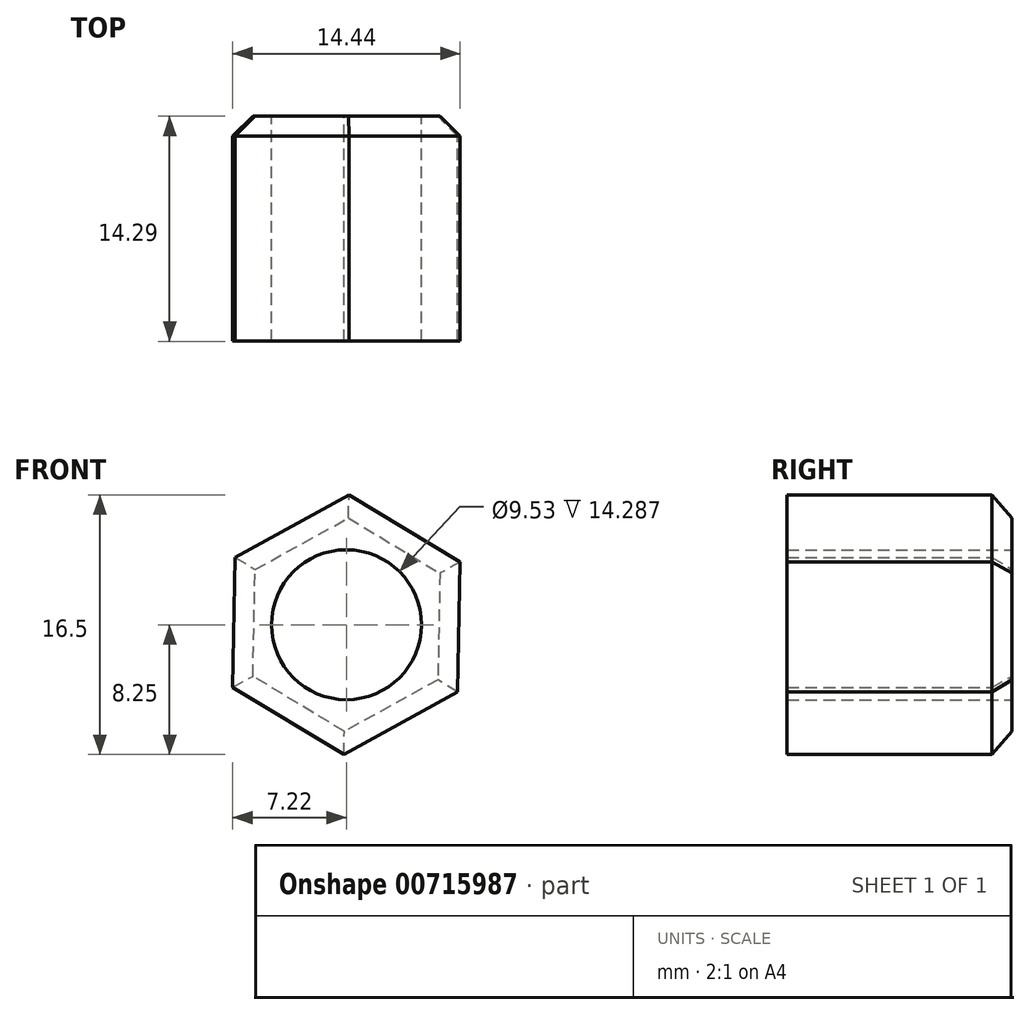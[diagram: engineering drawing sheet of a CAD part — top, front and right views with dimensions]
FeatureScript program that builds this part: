
annotation { "Feature Type Name" : "Feature", "Feature Type Description" : "" }
export const myFeature = defineFeature(function(context is Context, id is Id, definition is map)
    precondition{}
    {
        {
            var Q0;
            Q0=qCreatedBy(makeId("Front.planeOp"),FACE);
            var sketch = newSketch(context, id + "F0", { "sketchPlane" : qUnion([Q0])});
            skCircle(sketch, "E0.cCircle", {"center": v(0, 0) * mm, "radius": 7.14 * mm, "construction": true});
            skLineSegment(sketch, "E0.0", {"start": v(0.16, 8.25) * mm, "end": v(7.22, 3.98) * mm});
            skLineSegment(sketch, "E0.1", {"start": v(7.22, 3.98) * mm, "end": v(7.06, -4.26) * mm});
            skLineSegment(sketch, "E0.2", {"start": v(7.06, -4.26) * mm, "end": v(-0.16, -8.25) * mm});
            skLineSegment(sketch, "E0.3", {"start": v(-0.16, -8.25) * mm, "end": v(-7.22, -3.98) * mm});
            skLineSegment(sketch, "E0.4", {"start": v(-7.22, -3.98) * mm, "end": v(-7.06, 4.26) * mm});
            skLineSegment(sketch, "E0.5", {"start": v(-7.06, 4.26) * mm, "end": v(0.16, 8.25) * mm});
            skPoint(sketch, "E0.0.midPoint", {"position": v(3.7, 6.12) * mm});
            skCircle(sketch, "E1", {"center": v(0, 0) * mm, "radius": 4.76 * mm});
            skSolve(sketch);
        }
        {
            var Q0;
            Q0=makeQuery(id+"F0.imprint","IMPRINT",FACE,{"disambiguationData":[TD([[makeQuery(id+"F0.imprint","IMPRINT",EDGE,{"derivedFrom":sQuery(id+"F0.wireOp",EDGE,"E0.0")}),-1.0]])]});
            extrude(context, id + "F1", {"entities" : qUnion([Q0]), "depth" : 14.29 * mm, "offsetDistance" : 25.4 * mm});
        }
        {
            var Q0;
            Q0=makeQuery(id+"F1.opExtrude","CAP_EDGE",EDGE,{"disambiguationData":[OSD([sQuery(id+"F0.wireOp",EDGE,"E0.5")])],"isStart":true});
            var Q1;
            Q1=makeQuery(id+"F1.opExtrude","CAP_EDGE",EDGE,{"disambiguationData":[OSD([sQuery(id+"F0.wireOp",EDGE,"E0.1")])],"isStart":true});
            var Q2;
            Q2=makeQuery(id+"F1.opExtrude","CAP_EDGE",EDGE,{"disambiguationData":[OSD([sQuery(id+"F0.wireOp",EDGE,"E0.0")])],"isStart":true});
            var Q3;
            Q3=makeQuery(id+"F1.opExtrude","CAP_EDGE",EDGE,{"disambiguationData":[OSD([sQuery(id+"F0.wireOp",EDGE,"E0.2")])],"isStart":true});
            var Q4;
            Q4=makeQuery(id+"F1.opExtrude","CAP_EDGE",EDGE,{"disambiguationData":[OSD([sQuery(id+"F0.wireOp",EDGE,"E0.3")])],"isStart":true});
            var Q5;
            Q5=makeQuery(id+"F1.opExtrude","CAP_EDGE",EDGE,{"disambiguationData":[OSD([sQuery(id+"F0.wireOp",EDGE,"E0.4")])],"isStart":true});
            chamfer(context, id + "F2", {"entities" : qUnion([Q0, Q1, Q2, Q3, Q4, Q5]), "width" : 1.27 * mm, "tangentPropagation" : true});
        }
    });
